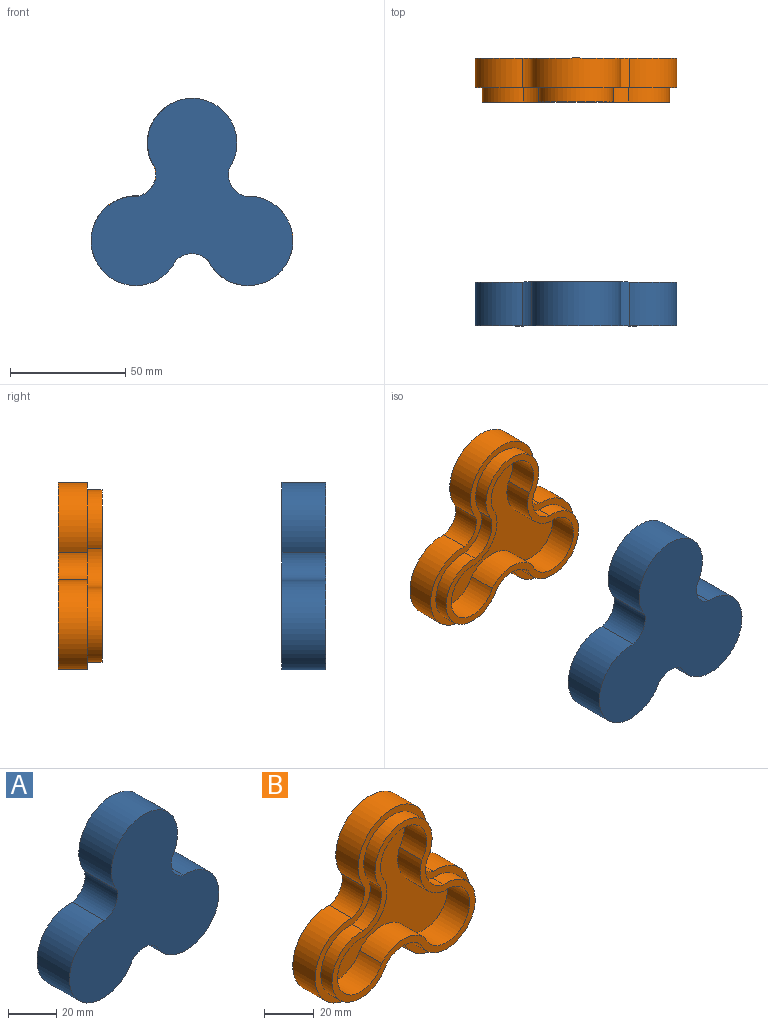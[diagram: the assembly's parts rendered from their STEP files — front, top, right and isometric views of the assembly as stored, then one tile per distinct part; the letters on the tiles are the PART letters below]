
ASSEMBLY  parts=2 mates=1
PART A: 22 faces, bbox 87.7x19.1x81.3 mm
  f0: cylinder r=9.73mm len=19.05mm, axis (0,-1,0), area 298.5mm2, adj f1,f11,f12,f13
  f1: cylinder r=19.43mm len=38.86mm, axis (0,-1,0), area 1601.7mm2, adj f0,f2,f12,f13
  f2: cylinder r=9.88mm len=19.05mm, axis (0,-1,0), area 300.7mm2, adj f1,f3,f12,f13
  f3: cylinder r=19.43mm len=38.86mm, axis (0,-1,0), area 1600.7mm2, adj f2,f4,f12,f13
  f4: cylinder r=9.73mm len=19.05mm, axis (0,-1,0), area 296mm2, adj f3,f11,f12,f13
  f5: cylinder r=16.27mm len=32.54mm, axis (0,-1,0), area 452.5mm2, adj f6,f10,f12,f20
  f6: cylinder r=13.04mm len=16.84mm, axis (0,-1,0), area 139.4mm2, adj f5,f7,f12,f20
  f7: cylinder r=16.27mm len=32.54mm, axis (0,-1,0), area 452.6mm2, adj f6,f8,f12,f20
  f8: cylinder r=12.89mm len=16.82mm, axis (0,-1,0), area 138.8mm2, adj f7,f9,f12,f20
  f9: cylinder r=16.27mm len=32.54mm, axis (0,-1,0), area 452.5mm2, adj f8,f10,f12,f20
  f10: cylinder r=12.89mm len=19.23mm, axis (0,-1,0), area 137.8mm2, adj f5,f9,f12,f20
  f11: cylinder r=19.43mm len=38.86mm, axis (0,-1,0), area 1600.5mm2, adj f0,f4,f12,f13
  f12: plane 87.7x81.34mm, normal (0,1,0), area 913.8mm2, adj f0,f1,f2,f3,f4,f5,f6,f7
  f13: plane 87.7x81.34mm, normal (0,-1,0), area 4207.8mm2, adj f0,f1,f2,f3,f4,f11
  f14: cylinder r=13.08mm len=26.16mm, axis (0,-1,0), area 369.2mm2, adj f15,f19,f20,f21
  f15: cylinder r=16.08mm len=21.57mm, axis (0,-1,0), area 179.8mm2, adj f14,f16,f20,f21
  f16: cylinder r=13.08mm len=26.16mm, axis (0,-1,0), area 369.2mm2, adj f15,f17,f20,f21
  f17: cylinder r=16.08mm len=24.69mm, axis (0,-1,0), area 178.7mm2, adj f16,f18,f20,f21
  f18: cylinder r=13.08mm len=26.16mm, axis (0,-1,0), area 369.2mm2, adj f17,f19,f20,f21
  f19: cylinder r=16.23mm len=21.57mm, axis (0,-1,0), area 180.3mm2, adj f14,f18,f20,f21
  f20: plane 81.38x75.02mm, normal (0,1,0), area 859.1mm2, adj f5,f6,f7,f8,f9,f10,f14,f15
  f21: plane 75x68.64mm, normal (0,1,0), area 2434.9mm2, adj f14,f15,f16,f17,f18,f19
PART B: 22 faces, bbox 87.8x19.1x81.3 mm
  f0: plane 81.35x74.89mm, normal (0,-1,0), area 847.7mm2, adj f1,f2,f3,f4,f5,f6,f8,f9
  f1: cylinder r=13.08mm len=26.16mm, axis (0,1,0), area 738.5mm2, adj f0,f2,f6,f7
  f2: cylinder r=16.08mm len=21.52mm, axis (0,1,0), area 360.5mm2, adj f0,f1,f3,f7
  f3: cylinder r=13.08mm len=26.16mm, axis (0,1,0), area 740.4mm2, adj f0,f2,f4,f7
  f4: cylinder r=16.08mm len=24.69mm, axis (0,1,0), area 357.5mm2, adj f0,f3,f5,f7
  f5: cylinder r=13.08mm len=26.16mm, axis (0,1,0), area 738.5mm2, adj f0,f4,f6,f7
  f6: cylinder r=16.08mm len=21.38mm, axis (0,1,0), area 357.5mm2, adj f0,f1,f5,f7
  f7: plane 75.05x68.59mm, normal (0,-1,0), area 2432mm2, adj f1,f2,f3,f4,f5,f6
  f8: cylinder r=16.23mm len=32.46mm, axis (0,-1,0), area 451.5mm2, adj f0,f9,f13,f14
  f9: cylinder r=12.93mm len=16.84mm, axis (0,-1,0), area 139.7mm2, adj f0,f8,f10,f14
  f10: cylinder r=16.23mm len=32.46mm, axis (0,-1,0), area 452.6mm2, adj f0,f9,f11,f14
  f11: cylinder r=12.93mm len=19.29mm, axis (0,-1,0), area 138.2mm2, adj f0,f10,f12,f14
  f12: cylinder r=16.23mm len=32.46mm, axis (0,-1,0), area 451.4mm2, adj f0,f11,f13,f14
  f13: cylinder r=12.93mm len=16.71mm, axis (0,-1,0), area 138.3mm2, adj f0,f8,f12,f14
  f14: plane 87.75x81.29mm, normal (0,-1,0), area 925.1mm2, adj f8,f9,f10,f11,f12,f13,f16,f17
  f15: plane 87.75x81.29mm, normal (0,1,0), area 4204.8mm2, adj f16,f17,f18,f19,f20,f21
  f16: cylinder r=19.43mm len=38.86mm, axis (0,1,0), area 1069.7mm2, adj f14,f15,f17,f21
  f17: cylinder r=9.73mm len=13.92mm, axis (0,1,0), area 196.9mm2, adj f14,f15,f16,f18
  f18: cylinder r=19.43mm len=38.86mm, axis (0,1,0), area 1067.1mm2, adj f14,f15,f17,f19
  f19: cylinder r=9.73mm len=12.7mm, axis (0,1,0), area 197.3mm2, adj f14,f15,f18,f20
  f20: cylinder r=19.43mm len=38.86mm, axis (0,1,0), area 1067.5mm2, adj f14,f15,f19,f21
  f21: cylinder r=9.73mm len=12.7mm, axis (0,1,0), area 199.6mm2, adj f14,f15,f16,f20
PLACE A t=(-168.34,-54.53,-5.5)mm
PLACE B t=(-48.51,61.77,-5.5)mm fixed
MATE slider A.f2 <-> B.f6  axis (0,-1,0) through (-74.01,-35.48,34.86)mm
